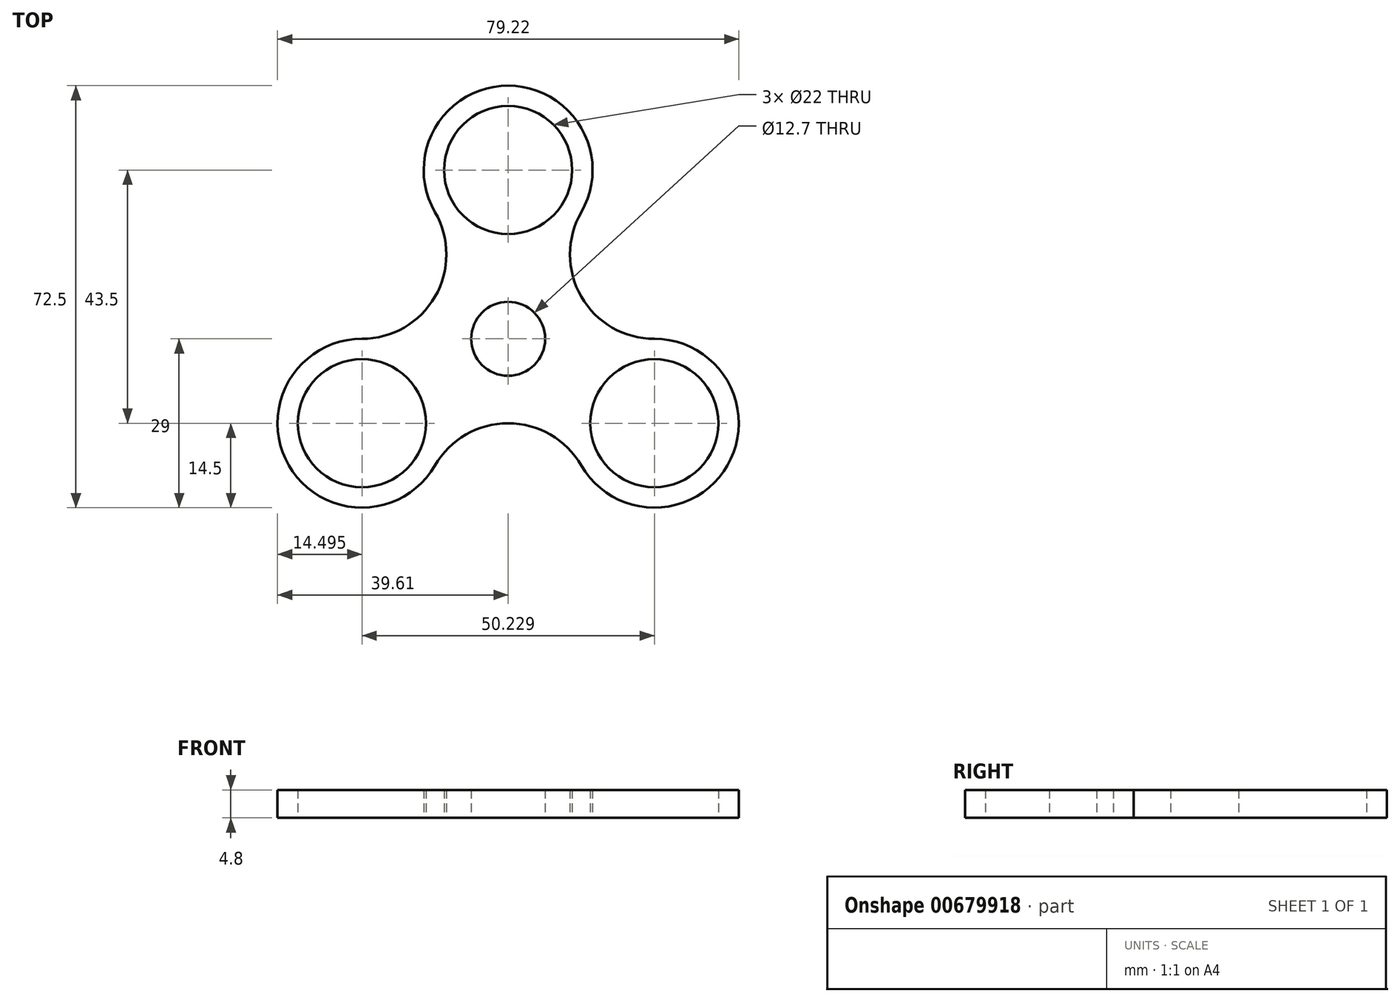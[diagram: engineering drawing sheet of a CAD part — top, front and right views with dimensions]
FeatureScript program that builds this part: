
annotation { "Feature Type Name" : "Feature", "Feature Type Description" : "" }
export const myFeature = defineFeature(function(context is Context, id is Id, definition is map)
    precondition{}
    {
        {
            var Q0;
            Q0=qCreatedBy(makeId("Top.planeOp"),FACE);
            var sketch = newSketch(context, id + "F0", { "sketchPlane" : qUnion([Q0])});
            skCircle(sketch, "E0", {"center": v(0, 0) * mm, "radius": 6.35 * mm});
            skCircle(sketch, "E1", {"center": v(0, 0) * mm, "radius": 14.5 * mm});
            skCircle(sketch, "E2", {"center": v(0, 29) * mm, "radius": 11 * mm});
            skArc(sketch, "E3", {"start": v(12.56, 21.75) * mm, "mid": v(0, 43.5) * mm, "end": v(-12.56, 21.75) * mm});
            skArc(sketch, "E4", {"start": v(-12.56, 7.25) * mm, "mid": v(-10.61, 14.5) * mm, "end": v(-12.56, 21.75) * mm});
            skArc(sketch, "E5", {"start": v(12.56, 21.75) * mm, "mid": v(10.61, 14.5) * mm, "end": v(12.56, 7.25) * mm});
            skArc(sketch, "E6.1.0", {"start": v(-25.11, 0) * mm, "mid": v(-37.67, -21.75) * mm, "end": v(-12.56, -21.75) * mm});
            skCircle(sketch, "E6.1.1", {"center": v(-25.11, -14.5) * mm, "radius": 11 * mm});
            skArc(sketch, "E6.1.2", {"start": v(0, -14.5) * mm, "mid": v(-7.25, -16.44) * mm, "end": v(-12.56, -21.75) * mm});
            skArc(sketch, "E6.1.3", {"start": v(-25.11, 0) * mm, "mid": v(-17.86, 1.94) * mm, "end": v(-12.56, 7.25) * mm});
            skArc(sketch, "E6.2.0", {"start": v(12.56, -21.75) * mm, "mid": v(37.67, -21.75) * mm, "end": v(25.11, 0) * mm});
            skCircle(sketch, "E6.2.1", {"center": v(25.11, -14.5) * mm, "radius": 11 * mm});
            skArc(sketch, "E6.2.2", {"start": v(12.56, 7.25) * mm, "mid": v(17.86, 1.94) * mm, "end": v(25.11, 0) * mm});
            skArc(sketch, "E6.2.3", {"start": v(12.56, -21.75) * mm, "mid": v(7.25, -16.44) * mm, "end": v(0, -14.5) * mm});
            skSolve(sketch);
        }
        {
            var Q0;
            Q0 = qSketchRegion(id + "F0", true);
            extrude(context, id + "F1", {"entities" : qUnion([Q0]), "depth" : 4.8 * mm, "offsetDistance" : 25 * mm});
        }
    });
